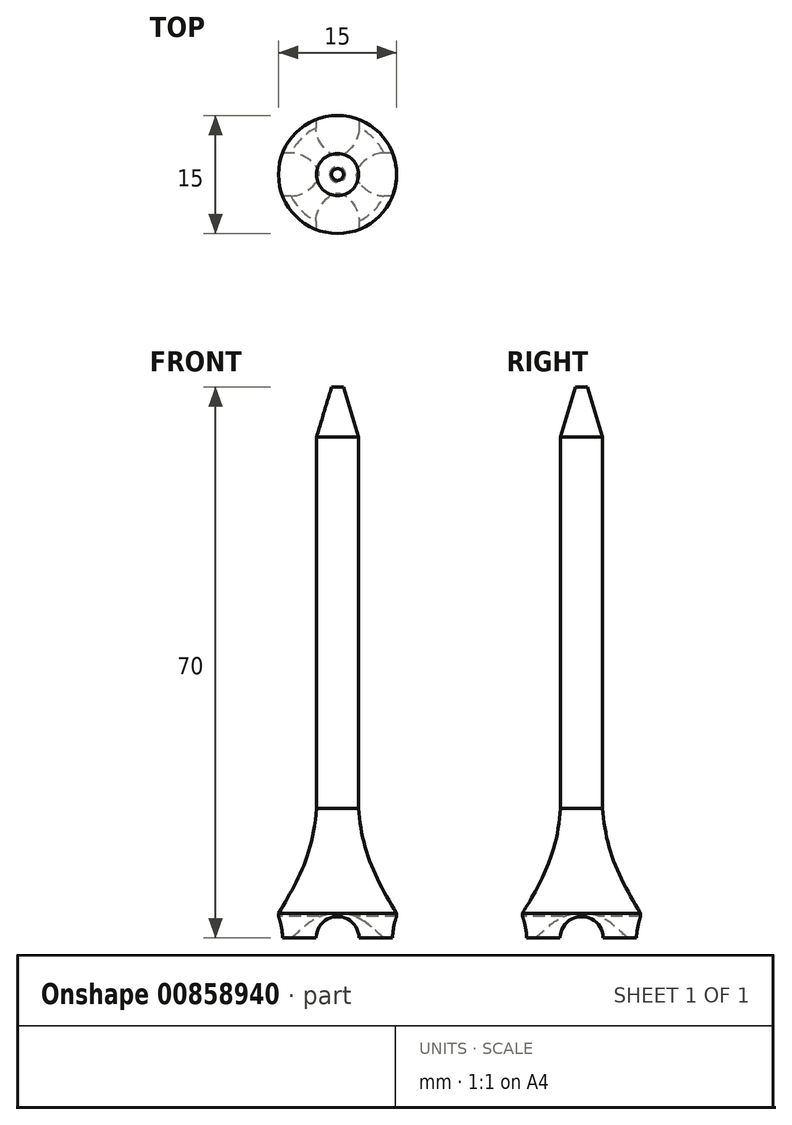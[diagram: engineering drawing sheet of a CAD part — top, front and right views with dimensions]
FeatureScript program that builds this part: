
annotation { "Feature Type Name" : "Feature", "Feature Type Description" : "" }
export const myFeature = defineFeature(function(context is Context, id is Id, definition is map)
    precondition{}
    {
        {
            var Q0;
            Q0=qCreatedBy(makeId("Front.planeOp"),FACE);
            var sketch = newSketch(context, id + "F0", { "sketchPlane" : qUnion([Q0])});
            skLineSegment(sketch, "E0", {"start": v(0, 0) * mm, "end": v(0, 70) * mm});
            skLineSegment(sketch, "E1", {"start": v(7.5, 0) * mm, "end": v(7.5, 3.15) * mm});
            skLineSegment(sketch, "E2", {"start": v(0, 3.15) * mm, "end": v(1, 3.15) * mm});
            skLineSegment(sketch, "E3", {"start": v(7.5, 0) * mm, "end": v(6.5, 0) * mm});
            skLineSegment(sketch, "E4", {"start": v(0, 70) * mm, "end": v(0.75, 70) * mm});
            skLineSegment(sketch, "E5", {"start": v(2.67, 63.65) * mm, "end": v(2.68, 16.5) * mm});
            skFitSpline(sketch, "E6", {"points": [v(7.5, 3.15) * mm, v(2.68, 16.5) * mm, v(14, 67.7) * mm], "startDerivative": vector(-19.46, 32.36) * mm, "endDerivative": vector(27.53, 90.6) * mm});
            skLineSegment(sketch, "E7", {"start": v(2.68, 63.65) * mm, "end": v(0.75, 70) * mm});
            skFitSpline(sketch, "E8", {"points": [v(1, 3.15) * mm, v(4, 2) * mm, v(6.5, 0) * mm], "startDerivative": vector(6.25, -1.85) * mm, "endDerivative": vector(4.75, -4.45) * mm});
            skSolve(sketch);
        }
        {
            var Q0;
            Q0 = qSketchRegion(id + "F0", true);
            var Q1;
            Q1=sQuery(id+"F0.wireOp",EDGE,"E0");
            revolve(context, id + "F1", {"surfaceOperationType" : NewSurfaceOperationType.NEW, "entities" : qUnion([Q0]), "axis" : qUnion([Q1]), "revolveType" : RevolveType.FULL});
        }
        {
            var Q0;
            Q0=qCreatedBy(makeId("Front.planeOp"),FACE);
            var sketch = newSketch(context, id + "F2", { "sketchPlane" : qUnion([Q0])});
            skCircle(sketch, "E9", {"center": v(0, 0) * mm, "radius": 2.73 * mm});
            skSolve(sketch);
        }
        {
            var Q0;
            Q0 = qSketchRegion(id + "F2", true);
            extrude(context, id + "F3", {"entities" : qUnion([Q0]), "operationType" : NewBodyOperationType.REMOVE, "endBound" : BoundingType.SYMMETRIC, "oppositeDirection" : true, "depth" : 15 * mm, "offsetDistance" : 25 * mm});
        }
        {
            var Q0;
            Q0=qCreatedBy(makeId("Right.planeOp"),FACE);
            var sketch = newSketch(context, id + "F4", { "sketchPlane" : qUnion([Q0])});
            skCircle(sketch, "E10", {"center": v(0, 0) * mm, "radius": 2.73 * mm});
            skSolve(sketch);
        }
        {
            var Q0;
            Q0 = qSketchRegion(id + "F4", true);
            extrude(context, id + "F5", {"entities" : qUnion([Q0]), "operationType" : NewBodyOperationType.REMOVE, "endBound" : BoundingType.SYMMETRIC, "depth" : 15 * mm, "offsetDistance" : 25 * mm});
        }
    });
